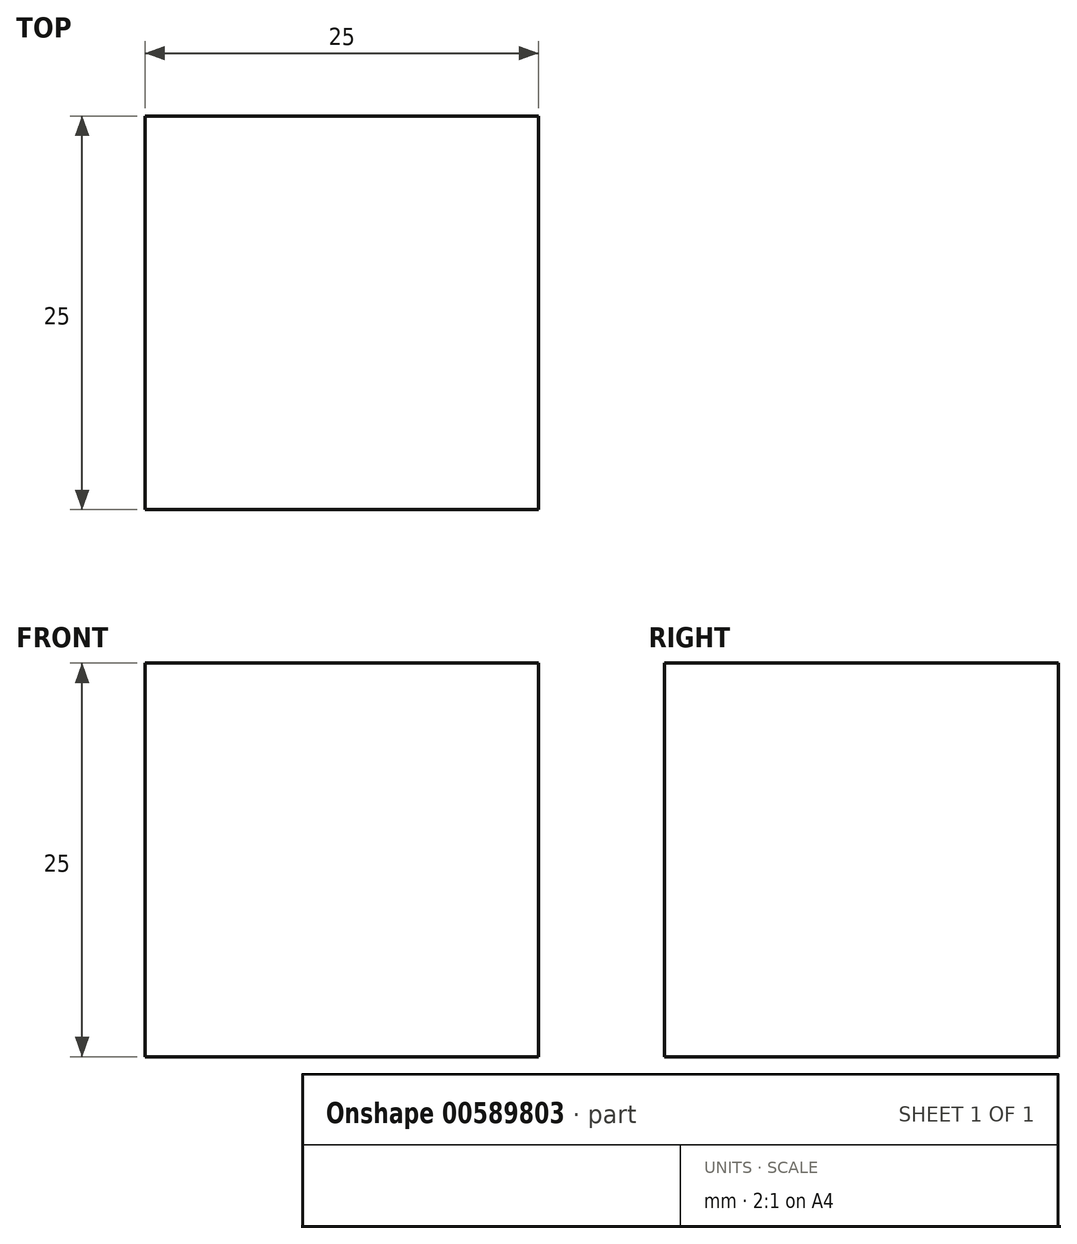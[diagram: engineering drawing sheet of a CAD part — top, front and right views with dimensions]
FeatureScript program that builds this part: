
annotation { "Feature Type Name" : "Feature", "Feature Type Description" : "" }
export const myFeature = defineFeature(function(context is Context, id is Id, definition is map)
    precondition{}
    {
        {
            var Q0;
            Q0=qCreatedBy(makeId("Top.planeOp"),FACE);
            var sketch = newSketch(context, id + "F0", { "sketchPlane" : qUnion([Q0])});
            skLineSegment(sketch, "E0.bottom", {"start": v(0, 0) * mm, "end": v(-25, 0) * mm});
            skLineSegment(sketch, "E0.top", {"start": v(0, 25) * mm, "end": v(-25, 25) * mm});
            skLineSegment(sketch, "E0.left", {"start": v(0, 0) * mm, "end": v(0, 25) * mm});
            skLineSegment(sketch, "E0.right", {"start": v(-25, 0) * mm, "end": v(-25, 25) * mm});
            skSolve(sketch);
        }
        {
            var Q0;
            Q0 = qSketchRegion(id + "F0", true);
            extrude(context, id + "F1", {"entities" : qUnion([Q0]), "depth" : 25 * mm, "offsetDistance" : 25 * mm});
        }
    });
